# Revit family: Flex
name_source: partatom
category: Мебель
revit_build: Autodesk Revit 2017 (Build: 20160225_1515(x64)
units: mm (PartAtom-declared; Revit-internal decimal feet)

## family parameters
Всегда вертикально = Да
Заголовок OmniClass = General Furniture and Specialties
На основе рабочей плоскости = Нет
Номер OmniClass = 23.40.20.00
Общий = Нет
При загрузке вырезать с полостями = Нет
Точка расчета площади = Нет

## types (9) — shared parameters
Seat = Skandiform Flex Seat
Изготовитель = Skandiform AB
Ключевая пометка = XBF.2
Комментарии к типоразмеру = Created by Astacus AB
Описание = S-028 and KS-128 chassis in chromium or silver lacquered metal. F-228 and F-229 chassis in chromium. Armrests in black TPE.

## per-type parameters (varying)
| type | Flex Leg | Leg | URL | Группа модели |
| Flex F-229 Chrome | Flex-leg-f229 | Skandiform Flex Chrome | http://www.biminfo.se | F-229 |
| Flex F-228 Chrome | Flex-leg-f228 | Skandiform Flex Chrome | http://www.biminfo.se | F-288 |
| Flex KS-128 Chrome | Flex-leg-ks128 | Skandiform Flex Chrome | http://www.biminfo.se | KS-128 |
| Flex S-028 Chromium | Flex-leg-s028 | Skandiform Flex Chrome | http://www.biminfo.se | S-028 |
| Flex KS-128 Silver | Flex-leg-ks128 | Skandiform Flex Silver | http://www.biminfo.se | KS-128 |
| Flex S-028 Silver | Flex-leg-s028 | Skandiform Flex Silver | http://www.biminfo.se | S-028 |
| Flex KS-198 Silver | Flex-leg-ks198 | Skandiform Flex Silver | http://www.biminfo.se | KS-198 |
| Flex KS-198 Chrome | Flex-leg-ks198 | Skandiform Flex Chrome | http://file-system.ru | KS-198 |
| Flex F-238 Chrome | Flex-leg-f228 | Skandiform Flex Chrome | http://www.biminfo.se | F-288 |

## geometry (parser evidence)
native form markers: Blend x13, Sweep x39
no freeform markers — native parametric forms only
